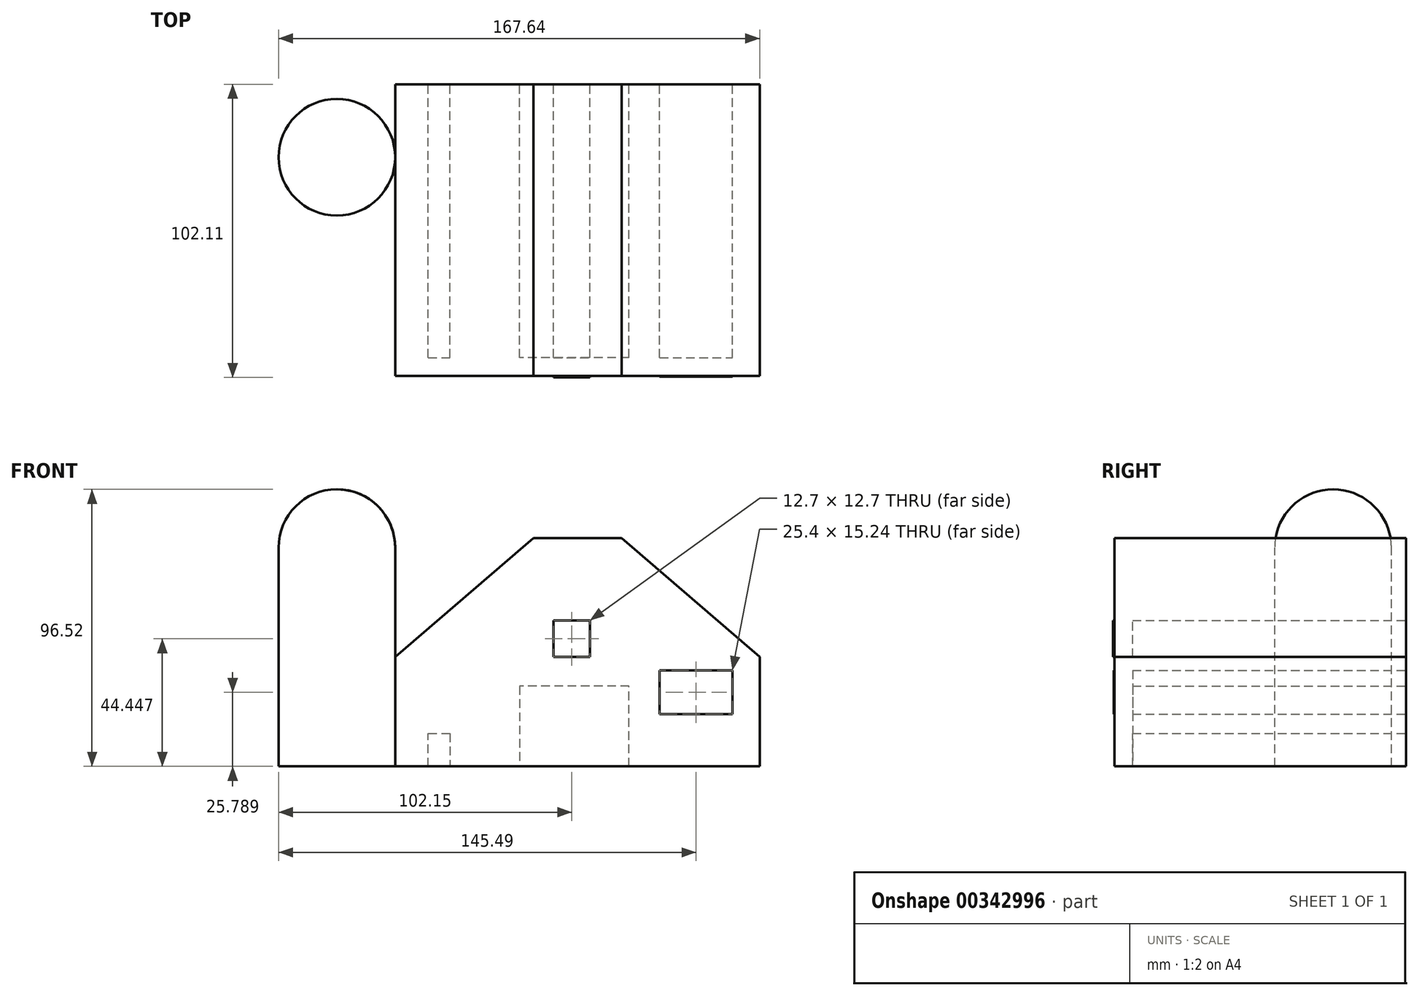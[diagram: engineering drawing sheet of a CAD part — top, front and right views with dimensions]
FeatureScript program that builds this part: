
annotation { "Feature Type Name" : "Feature", "Feature Type Description" : "" }
export const myFeature = defineFeature(function(context is Context, id is Id, definition is map)
    precondition{}
    {
        {
            var Q0;
            Q0=qCreatedBy(makeId("Front.planeOp"),FACE);
            var sketch = newSketch(context, id + "F0", { "sketchPlane" : qUnion([Q0])});
            skLineSegment(sketch, "E0", {"start": v(59.14, -7.08) * mm, "end": v(59.14, -45.18) * mm});
            skLineSegment(sketch, "E1", {"start": v(59.14, -45.18) * mm, "end": v(-67.86, -45.18) * mm});
            skLineSegment(sketch, "E2", {"start": v(-67.86, -45.18) * mm, "end": v(-67.86, -7.08) * mm});
            skLineSegment(sketch, "E3", {"start": v(-67.86, -7.08) * mm, "end": v(-19.72, 34.32) * mm});
            skLineSegment(sketch, "E4", {"start": v(-19.72, 34.32) * mm, "end": v(10.99, 34.32) * mm});
            skLineSegment(sketch, "E5", {"start": v(-67.86, -7.08) * mm, "end": v(59.14, -7.08) * mm});
            skLineSegment(sketch, "E6", {"start": v(-12.7, -7.08) * mm, "end": v(-12.7, 5.62) * mm});
            skLineSegment(sketch, "E7", {"start": v(-12.7, 5.62) * mm, "end": v(0, 5.62) * mm});
            skLineSegment(sketch, "E8", {"start": v(0, 5.62) * mm, "end": v(0, -7.08) * mm});
            skLineSegment(sketch, "E9", {"start": v(-56.37, -45.18) * mm, "end": v(-56.37, -33.75) * mm});
            skLineSegment(sketch, "E10", {"start": v(-56.37, -33.75) * mm, "end": v(-48.75, -33.75) * mm});
            skLineSegment(sketch, "E11", {"start": v(-48.75, -33.75) * mm, "end": v(-48.75, -45.18) * mm});
            skLineSegment(sketch, "E12", {"start": v(24.3, -11.77) * mm, "end": v(24.3, -27.01) * mm});
            skLineSegment(sketch, "E13", {"start": v(24.3, -27.01) * mm, "end": v(49.7, -27.01) * mm});
            skLineSegment(sketch, "E14", {"start": v(24.3, -11.77) * mm, "end": v(49.7, -11.77) * mm});
            skLineSegment(sketch, "E15", {"start": v(49.7, -11.77) * mm, "end": v(49.7, -27.01) * mm});
            skLineSegment(sketch, "E16", {"start": v(-56.37, -45.18) * mm, "end": v(-48.75, -45.18) * mm});
            skLineSegment(sketch, "E17", {"start": v(13.62, -45.18) * mm, "end": v(13.62, -17.24) * mm});
            skLineSegment(sketch, "E18", {"start": v(13.62, -17.24) * mm, "end": v(-24.48, -17.24) * mm});
            skLineSegment(sketch, "E19", {"start": v(-24.48, -17.24) * mm, "end": v(-24.48, -45.18) * mm});
            skLineSegment(sketch, "E20", {"start": v(-67.86, -45.18) * mm, "end": v(-67.86, 31.02) * mm});
            skLineSegment(sketch, "E21", {"start": v(-67.86, 31.02) * mm, "end": v(-88.18, 31.02) * mm});
            skLineSegment(sketch, "E22", {"start": v(-88.18, -45.18) * mm, "end": v(-67.86, -45.18) * mm});
            skArc(sketch, "E23", {"start": v(-67.86, 31.02) * mm, "mid": v(-73.82, 45.39) * mm, "end": v(-88.18, 51.34) * mm});
            skLineSegment(sketch, "E24", {"start": v(-88.18, 51.34) * mm, "end": v(-88.18, -45.18) * mm});
            skPoint(sketch, "E25.orphan", {"position": v(-108.5, -45.18) * mm});
            skPoint(sketch, "E26.start.orphan", {"position": v(10.99, 33.28) * mm});
            skLineSegment(sketch, "E27", {"start": v(10.99, 34.32) * mm, "end": v(59.14, -7.08) * mm});
            skSolve(sketch);
        }
        {
            var Q0;
            {var subQ7=sQuery(id+"F0.wireOp",EDGE,"E0");Q0=makeQuery(id+"F0.imprint","IMPRINT",FACE,{"disambiguationData":[TD([[makeQuery(id+"F0.imprint","IMPRINT",EDGE,{"derivedFrom":subQ7}),-1.0]])]});}
            var Q1;
            {var subQ1=sQuery(id+"F0.wireOp",EDGE,"E3");Q1=makeQuery(id+"F0.imprint","IMPRINT",FACE,{"disambiguationData":[TD([[makeQuery(id+"F0.imprint","IMPRINT",EDGE,{"derivedFrom":subQ1}),-1.0]])]});}
            extrude(context, id + "F1", {"entities" : qUnion([Q0, Q1]), "depth" : 76.2 * mm, "hasSecondDirection" : true, "secondDirectionOppositeDirection" : true, "secondDirectionDepth" : 25.4 * mm});
        }
        {
            var Q0;
            {var subQ0=sQuery(id+"F0.wireOp",EDGE,"E21");Q0=makeQuery(id+"F0.imprint","IMPRINT",FACE,{"disambiguationData":[TD([[makeQuery(id+"F0.imprint","IMPRINT",EDGE,{"derivedFrom":subQ0}),-1.0]])]});}
            var Q1;
            {var subQ1=sQuery(id+"F0.wireOp",EDGE,"E21");Q1=makeQuery(id+"F0.imprint","IMPRINT",FACE,{"disambiguationData":[TD([[makeQuery(id+"F0.imprint","IMPRINT",EDGE,{"derivedFrom":subQ1}),1.0]])]});}
            var Q2;
            Q2=sQuery(id+"F0.wireOp",EDGE,"E24");
            revolve(context, id + "F2", {"entities" : qUnion([Q0, Q1]), "axis" : qUnion([Q2]), "revolveType" : RevolveType.FULL});
        }
        {
            var Q0;
            {var subQ0=sQuery(id+"F0.wireOp",EDGE,"E17");Q0=makeQuery(id+"F0.imprint","IMPRINT",FACE,{"disambiguationData":[TD([[makeQuery(id+"F0.imprint","IMPRINT",EDGE,{"derivedFrom":subQ0}),1.0]])]});}
            extrude(context, id + "F3", {"entities" : qUnion([Q0]), "operationType" : NewBodyOperationType.ADD, "depth" : 76.2 * mm, "hasSecondDirection" : true, "secondDirectionOppositeDirection" : false, "secondDirectionDepth" : 69.85 * mm});
        }
        {
            var Q0;
            Q0=makeQuery(id+"F0.imprint","IMPRINT",FACE,{"disambiguationData":[TD([[makeQuery(id+"F0.imprint","IMPRINT",EDGE,{"derivedFrom":sQuery(id+"F0.wireOp",EDGE,"E9")}),-1.0]])]});
            extrude(context, id + "F4", {"entities" : qUnion([Q0]), "operationType" : NewBodyOperationType.ADD, "depth" : 76.2 * mm, "hasSecondDirection" : true, "secondDirectionOppositeDirection" : false, "secondDirectionDepth" : 69.85 * mm});
        }
        {
            var Q0;
            {var subQ0=sQuery(id+"F0.wireOp",EDGE,"E6");Q0=makeQuery(id+"F0.imprint","IMPRINT",FACE,{"disambiguationData":[TD([[makeQuery(id+"F0.imprint","IMPRINT",EDGE,{"derivedFrom":subQ0}),-1.0]])]});}
            extrude(context, id + "F5", {"entities" : qUnion([Q0]), "operationType" : NewBodyOperationType.ADD, "depth" : 76.7 * mm, "hasSecondDirection" : true, "secondDirectionOppositeDirection" : false, "secondDirectionDepth" : 69.85 * mm});
        }
        {
            var Q0;
            Q0=makeQuery(id+"F0.imprint","IMPRINT",FACE,{"disambiguationData":[TD([[makeQuery(id+"F0.imprint","IMPRINT",EDGE,{"derivedFrom":sQuery(id+"F0.wireOp",EDGE,"E12")}),1.0]])]});
            extrude(context, id + "F6", {"entities" : qUnion([Q0]), "operationType" : NewBodyOperationType.ADD, "depth" : 76.45 * mm, "hasSecondDirection" : true, "secondDirectionOppositeDirection" : false, "secondDirectionDepth" : 69.85 * mm});
        }
    });
